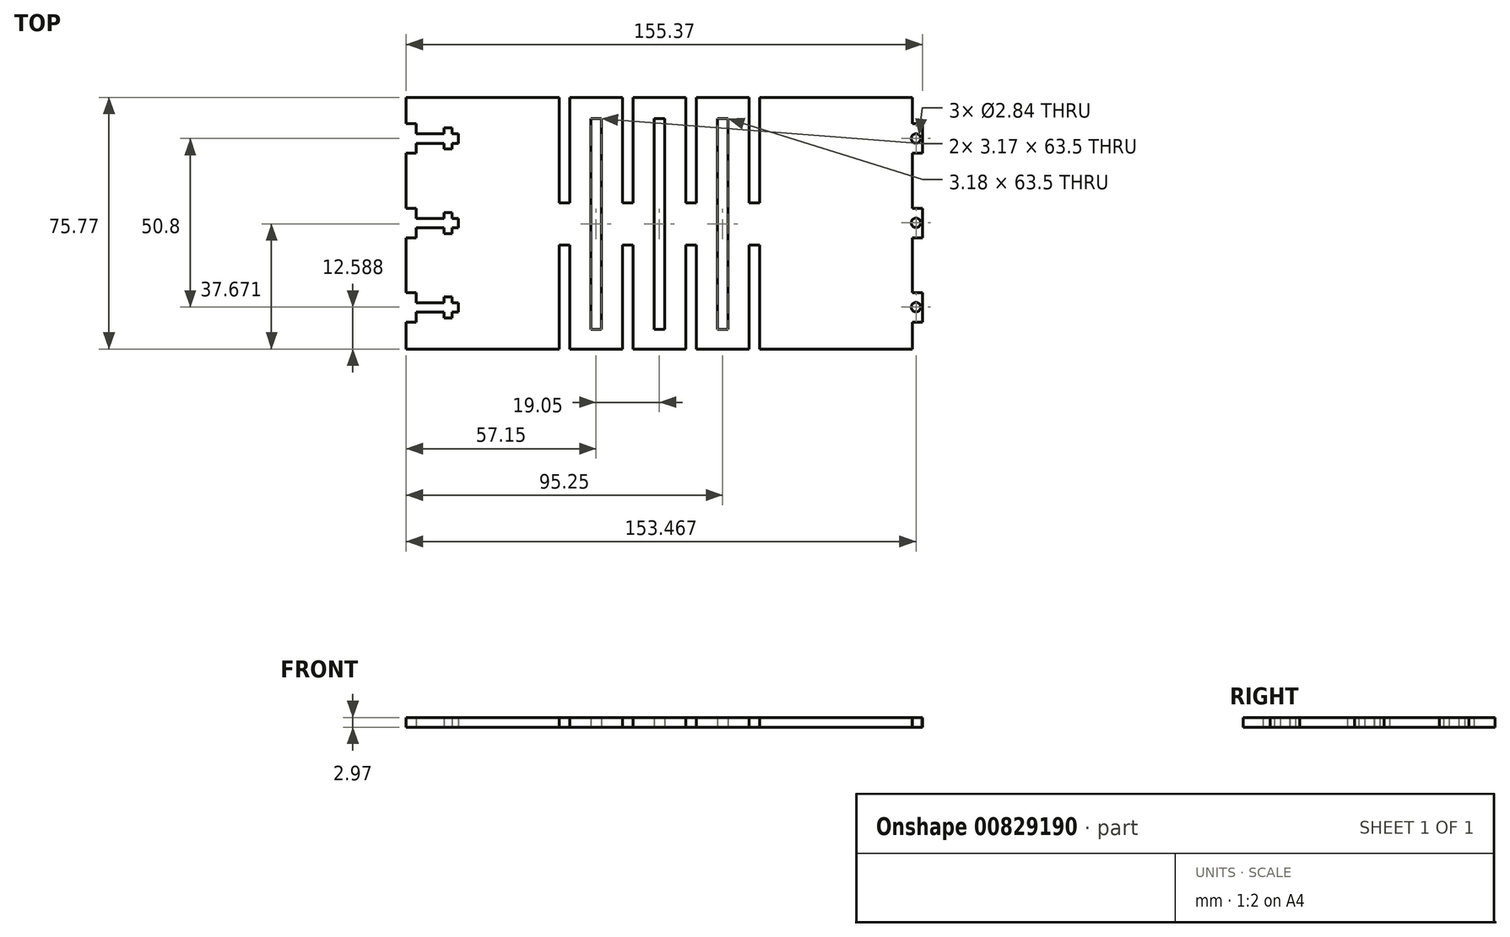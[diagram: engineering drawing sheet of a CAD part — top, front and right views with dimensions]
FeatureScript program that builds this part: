
annotation { "Feature Type Name" : "Feature", "Feature Type Description" : "" }
export const myFeature = defineFeature(function(context is Context, id is Id, definition is map)
    precondition{}
    {
        {
            var Q0;
            Q0=qCreatedBy(makeId("Top.planeOp"),FACE);
            var sketch = newSketch(context, id + "F0", { "sketchPlane" : qUnion([Q0])});
            skLineSegment(sketch, "E0.bottom", {"start": v(0, 0) * mm, "end": v(152.4, 0) * mm});
            skLineSegment(sketch, "E0.top", {"start": v(0, 75.77) * mm, "end": v(152.4, 75.77) * mm});
            skLineSegment(sketch, "E0.left", {"start": v(0, 0) * mm, "end": v(0, 8.04) * mm});
            skLineSegment(sketch, "E0.right", {"start": v(152.4, 0) * mm, "end": v(152.4, 8.04) * mm});
            skLineSegment(sketch, "E1", {"start": v(76.2, 75.77) * mm, "end": v(76.2, 0) * mm, "construction": true});
            skLineSegment(sketch, "E2.bottom", {"start": v(74.61, 69.42) * mm, "end": v(77.79, 69.42) * mm});
            skLineSegment(sketch, "E2.top", {"start": v(74.61, 5.92) * mm, "end": v(77.79, 5.92) * mm});
            skLineSegment(sketch, "E2.left", {"start": v(74.61, 69.42) * mm, "end": v(74.61, 5.92) * mm});
            skLineSegment(sketch, "E2.right", {"start": v(77.79, 69.42) * mm, "end": v(77.79, 5.92) * mm});
            skLineSegment(sketch, "E3.bottom", {"start": v(84.14, 0) * mm, "end": v(87.31, 0) * mm});
            skLineSegment(sketch, "E3.top", {"start": v(84.14, 75.77) * mm, "end": v(87.31, 75.77) * mm});
            skLineSegment(sketch, "E3.left", {"start": v(84.14, 0) * mm, "end": v(84.14, 31.32) * mm});
            skLineSegment(sketch, "E3.right", {"start": v(87.31, 0) * mm, "end": v(87.31, 31.32) * mm});
            skLineSegment(sketch, "E4", {"start": v(84.14, 31.32) * mm, "end": v(87.31, 31.32) * mm});
            skLineSegment(sketch, "E5", {"start": v(84.14, 44.02) * mm, "end": v(87.31, 44.02) * mm});
            skLineSegment(sketch, "E6.trimOffspring", {"start": v(84.14, 44.02) * mm, "end": v(84.14, 75.77) * mm});
            skLineSegment(sketch, "E7.trimOffspring", {"start": v(87.31, 44.02) * mm, "end": v(87.31, 75.77) * mm});
            skLineSegment(sketch, "E8.1.0.0", {"start": v(93.66, 69.42) * mm, "end": v(93.66, 5.92) * mm});
            skLineSegment(sketch, "E8.1.0.1", {"start": v(96.84, 69.42) * mm, "end": v(96.84, 5.92) * mm});
            skLineSegment(sketch, "E8.1.0.2", {"start": v(93.66, 5.92) * mm, "end": v(96.84, 5.92) * mm});
            skLineSegment(sketch, "E8.1.0.3", {"start": v(93.66, 69.42) * mm, "end": v(96.84, 69.42) * mm});
            skLineSegment(sketch, "E8.1.0.4", {"start": v(103.19, 44.02) * mm, "end": v(106.36, 44.02) * mm});
            skLineSegment(sketch, "E8.1.0.5", {"start": v(103.19, 44.02) * mm, "end": v(103.19, 75.77) * mm});
            skLineSegment(sketch, "E8.1.0.6", {"start": v(106.36, 44.02) * mm, "end": v(106.36, 75.77) * mm});
            skLineSegment(sketch, "E8.1.0.7", {"start": v(103.19, 75.77) * mm, "end": v(106.36, 75.77) * mm});
            skLineSegment(sketch, "E8.1.0.8", {"start": v(103.19, 31.32) * mm, "end": v(106.36, 31.32) * mm});
            skLineSegment(sketch, "E8.1.0.9", {"start": v(106.36, 0) * mm, "end": v(106.36, 31.32) * mm});
            skLineSegment(sketch, "E8.1.0.10", {"start": v(103.19, 0) * mm, "end": v(103.19, 31.32) * mm});
            skLineSegment(sketch, "E8.1.0.11", {"start": v(103.19, 0) * mm, "end": v(106.36, 0) * mm});
            skLineSegment(sketch, "E8.direction1", {"start": v(74.61, 5.92) * mm, "end": v(93.66, 5.92) * mm, "construction": true});
            skLineSegment(sketch, "E9.1.0.0", {"start": v(58.74, 69.42) * mm, "end": v(58.74, 5.92) * mm});
            skLineSegment(sketch, "E9.1.0.1", {"start": v(65.09, 31.32) * mm, "end": v(68.26, 31.32) * mm});
            skLineSegment(sketch, "E9.1.0.2", {"start": v(55.56, 69.42) * mm, "end": v(58.74, 69.42) * mm});
            skLineSegment(sketch, "E9.1.0.3", {"start": v(55.56, 69.42) * mm, "end": v(55.56, 5.92) * mm});
            skLineSegment(sketch, "E9.1.0.4", {"start": v(55.56, 5.92) * mm, "end": v(58.74, 5.92) * mm});
            skLineSegment(sketch, "E9.1.0.5", {"start": v(68.26, 0) * mm, "end": v(68.26, 31.32) * mm});
            skLineSegment(sketch, "E9.1.0.6", {"start": v(65.09, 0) * mm, "end": v(65.09, 31.32) * mm});
            skLineSegment(sketch, "E9.1.0.7", {"start": v(65.09, 0) * mm, "end": v(68.26, 0) * mm});
            skLineSegment(sketch, "E9.1.0.8", {"start": v(68.26, 44.02) * mm, "end": v(68.26, 75.77) * mm});
            skLineSegment(sketch, "E9.1.0.9", {"start": v(65.09, 44.02) * mm, "end": v(65.09, 75.77) * mm});
            skLineSegment(sketch, "E9.1.0.10", {"start": v(65.09, 44.02) * mm, "end": v(68.26, 44.02) * mm});
            skLineSegment(sketch, "E9.1.0.11", {"start": v(65.09, 75.77) * mm, "end": v(68.26, 75.77) * mm});
            skLineSegment(sketch, "E9.direction1", {"start": v(74.61, 5.92) * mm, "end": v(55.56, 5.92) * mm, "construction": true});
            skLineSegment(sketch, "E10.MirrorCS", {"start": v(49.21, 0) * mm, "end": v(46.04, 0) * mm});
            skLineSegment(sketch, "E11.MirrorCS", {"start": v(49.21, 0) * mm, "end": v(49.21, 31.32) * mm});
            skLineSegment(sketch, "E12.MirrorCS", {"start": v(46.04, 0) * mm, "end": v(46.04, 31.32) * mm});
            skLineSegment(sketch, "E13.MirrorCS", {"start": v(49.21, 31.32) * mm, "end": v(46.04, 31.32) * mm});
            skLineSegment(sketch, "E14.MirrorCS", {"start": v(49.21, 75.77) * mm, "end": v(46.04, 75.77) * mm});
            skLineSegment(sketch, "E15.MirrorCS", {"start": v(49.21, 44.02) * mm, "end": v(46.04, 44.02) * mm});
            skLineSegment(sketch, "E16.MirrorCS", {"start": v(49.21, 44.02) * mm, "end": v(49.21, 75.77) * mm});
            skLineSegment(sketch, "E17.MirrorCS", {"start": v(46.04, 44.02) * mm, "end": v(46.04, 75.77) * mm});
            skLineSegment(sketch, "E18.bottom", {"start": v(0, 67.83) * mm, "end": v(2.97, 67.83) * mm});
            skLineSegment(sketch, "E18.top", {"start": v(0, 58.94) * mm, "end": v(2.97, 58.94) * mm});
            skLineSegment(sketch, "E18.right", {"start": v(2.97, 67.83) * mm, "end": v(2.97, 64.81) * mm});
            skLineSegment(sketch, "E19", {"start": v(2.97, 63.39) * mm, "end": v(24.16, 63.39) * mm, "construction": true});
            skLineSegment(sketch, "E20.bottom", {"start": v(2.97, 64.81) * mm, "end": v(2.97, 64.81) * mm});
            skLineSegment(sketch, "E20.top", {"start": v(2.97, 61.97) * mm, "end": v(2.97, 61.97) * mm});
            skLineSegment(sketch, "E21.bottom", {"start": v(11.43, 66.56) * mm, "end": v(13.81, 66.56) * mm});
            skLineSegment(sketch, "E21.top", {"start": v(11.43, 60.21) * mm, "end": v(13.81, 60.21) * mm});
            skLineSegment(sketch, "E21.left", {"start": v(11.43, 66.56) * mm, "end": v(11.43, 64.81) * mm});
            skLineSegment(sketch, "E21.right", {"start": v(13.81, 66.56) * mm, "end": v(13.81, 64.81) * mm});
            skLineSegment(sketch, "E22.bottom", {"start": v(2.97, 64.81) * mm, "end": v(11.43, 64.81) * mm});
            skLineSegment(sketch, "E22.top", {"start": v(2.97, 61.97) * mm, "end": v(11.43, 61.97) * mm});
            skLineSegment(sketch, "E22.right", {"start": v(15.67, 64.81) * mm, "end": v(15.67, 61.97) * mm});
            skLineSegment(sketch, "E23.trimOffspring", {"start": v(2.97, 61.97) * mm, "end": v(2.97, 58.94) * mm});
            skLineSegment(sketch, "E24.trimOffspring", {"start": v(11.43, 61.97) * mm, "end": v(11.43, 60.21) * mm});
            skLineSegment(sketch, "E25.trimOffspring", {"start": v(13.81, 64.81) * mm, "end": v(15.67, 64.81) * mm});
            skLineSegment(sketch, "E26.trimOffspring", {"start": v(13.81, 61.97) * mm, "end": v(13.81, 60.21) * mm});
            skLineSegment(sketch, "E27.trimOffspring", {"start": v(13.81, 61.97) * mm, "end": v(15.67, 61.97) * mm});
            skLineSegment(sketch, "E28.0.1.0", {"start": v(0, 42.38) * mm, "end": v(2.97, 42.38) * mm});
            skLineSegment(sketch, "E28.0.1.1", {"start": v(2.97, 39.36) * mm, "end": v(11.43, 39.36) * mm});
            skLineSegment(sketch, "E28.0.1.2", {"start": v(2.97, 42.38) * mm, "end": v(2.97, 39.36) * mm});
            skLineSegment(sketch, "E28.0.1.3", {"start": v(11.43, 41.1) * mm, "end": v(11.43, 39.36) * mm});
            skLineSegment(sketch, "E28.0.1.4", {"start": v(11.43, 41.1) * mm, "end": v(13.81, 41.1) * mm});
            skLineSegment(sketch, "E28.0.1.5", {"start": v(13.81, 41.1) * mm, "end": v(13.81, 39.36) * mm});
            skLineSegment(sketch, "E28.0.1.6", {"start": v(13.81, 39.36) * mm, "end": v(15.67, 39.36) * mm});
            skLineSegment(sketch, "E28.0.1.7", {"start": v(15.67, 39.36) * mm, "end": v(15.67, 36.51) * mm});
            skLineSegment(sketch, "E28.0.1.8", {"start": v(13.81, 36.51) * mm, "end": v(15.67, 36.51) * mm});
            skLineSegment(sketch, "E28.0.1.9", {"start": v(13.81, 36.51) * mm, "end": v(13.81, 34.76) * mm});
            skLineSegment(sketch, "E28.0.1.10", {"start": v(11.43, 34.76) * mm, "end": v(13.81, 34.76) * mm});
            skLineSegment(sketch, "E28.0.1.11", {"start": v(11.43, 36.51) * mm, "end": v(11.43, 34.76) * mm});
            skLineSegment(sketch, "E28.0.1.12", {"start": v(2.97, 36.51) * mm, "end": v(11.43, 36.51) * mm});
            skLineSegment(sketch, "E28.0.1.13", {"start": v(2.97, 36.51) * mm, "end": v(2.97, 33.49) * mm});
            skLineSegment(sketch, "E28.0.1.14", {"start": v(0, 33.49) * mm, "end": v(2.97, 33.49) * mm});
            skLineSegment(sketch, "E28.0.2.0", {"start": v(0, 16.93) * mm, "end": v(2.97, 16.93) * mm});
            skLineSegment(sketch, "E28.0.2.1", {"start": v(2.97, 13.9) * mm, "end": v(11.43, 13.9) * mm});
            skLineSegment(sketch, "E28.0.2.2", {"start": v(2.97, 16.93) * mm, "end": v(2.97, 13.9) * mm});
            skLineSegment(sketch, "E28.0.2.3", {"start": v(11.43, 15.66) * mm, "end": v(11.43, 13.9) * mm});
            skLineSegment(sketch, "E28.0.2.4", {"start": v(11.43, 15.66) * mm, "end": v(13.81, 15.66) * mm});
            skLineSegment(sketch, "E28.0.2.5", {"start": v(13.81, 15.66) * mm, "end": v(13.81, 13.9) * mm});
            skLineSegment(sketch, "E28.0.2.6", {"start": v(13.81, 13.9) * mm, "end": v(15.67, 13.9) * mm});
            skLineSegment(sketch, "E28.0.2.7", {"start": v(15.67, 13.9) * mm, "end": v(15.67, 11.06) * mm});
            skLineSegment(sketch, "E28.0.2.8", {"start": v(13.81, 11.06) * mm, "end": v(15.67, 11.06) * mm});
            skLineSegment(sketch, "E28.0.2.9", {"start": v(13.81, 11.06) * mm, "end": v(13.81, 9.3) * mm});
            skLineSegment(sketch, "E28.0.2.10", {"start": v(11.43, 9.3) * mm, "end": v(13.81, 9.3) * mm});
            skLineSegment(sketch, "E28.0.2.11", {"start": v(11.43, 11.06) * mm, "end": v(11.43, 9.3) * mm});
            skLineSegment(sketch, "E28.0.2.12", {"start": v(2.97, 11.06) * mm, "end": v(11.43, 11.06) * mm});
            skLineSegment(sketch, "E28.0.2.13", {"start": v(2.97, 11.06) * mm, "end": v(2.97, 8.04) * mm});
            skLineSegment(sketch, "E28.0.2.14", {"start": v(0, 8.04) * mm, "end": v(2.97, 8.04) * mm});
            skLineSegment(sketch, "E28.direction1", {"start": v(0, 67.83) * mm, "end": v(25.4, 67.83) * mm, "construction": true});
            skLineSegment(sketch, "E28.direction2", {"start": v(0, 58.94) * mm, "end": v(0, 42.38) * mm, "construction": true});
            skLineSegment(sketch, "E29.trimOffspring", {"start": v(0, 67.83) * mm, "end": v(0, 75.77) * mm});
            skLineSegment(sketch, "E30.trimOffspring", {"start": v(0, 42.38) * mm, "end": v(0, 58.94) * mm});
            skLineSegment(sketch, "E31.trimOffspring", {"start": v(0, 16.93) * mm, "end": v(0, 33.49) * mm});
            skLineSegment(sketch, "E32.1.0.0", {"start": v(155.37, 67.83) * mm, "end": v(155.37, 64.81) * mm});
            skLineSegment(sketch, "E32.1.0.1", {"start": v(152.4, 67.83) * mm, "end": v(155.37, 67.83) * mm});
            skLineSegment(sketch, "E32.1.0.2", {"start": v(155.37, 61.97) * mm, "end": v(155.37, 58.94) * mm});
            skLineSegment(sketch, "E32.1.0.3", {"start": v(152.4, 58.94) * mm, "end": v(155.37, 58.94) * mm});
            skLineSegment(sketch, "E32.1.0.4", {"start": v(152.4, 42.38) * mm, "end": v(155.37, 42.38) * mm});
            skLineSegment(sketch, "E32.1.0.5", {"start": v(155.37, 42.38) * mm, "end": v(155.37, 39.36) * mm});
            skLineSegment(sketch, "E32.1.0.6", {"start": v(155.37, 36.51) * mm, "end": v(155.37, 33.49) * mm});
            skLineSegment(sketch, "E32.1.0.7", {"start": v(152.4, 33.49) * mm, "end": v(155.37, 33.49) * mm});
            skLineSegment(sketch, "E32.1.0.8", {"start": v(152.4, 16.93) * mm, "end": v(155.37, 16.93) * mm});
            skLineSegment(sketch, "E32.1.0.9", {"start": v(155.37, 16.93) * mm, "end": v(155.37, 13.9) * mm});
            skLineSegment(sketch, "E32.1.0.10", {"start": v(155.37, 11.06) * mm, "end": v(155.37, 8.04) * mm});
            skLineSegment(sketch, "E32.1.0.11", {"start": v(152.4, 8.04) * mm, "end": v(155.37, 8.04) * mm});
            skLineSegment(sketch, "E32.direction1", {"start": v(2.97, 64.81) * mm, "end": v(155.37, 64.81) * mm, "construction": true});
            skLineSegment(sketch, "E33", {"start": v(155.37, 64.81) * mm, "end": v(155.37, 61.97) * mm});
            skLineSegment(sketch, "E34", {"start": v(155.37, 39.36) * mm, "end": v(155.37, 36.51) * mm});
            skLineSegment(sketch, "E35", {"start": v(155.37, 13.9) * mm, "end": v(155.37, 11.06) * mm});
            skCircle(sketch, "E36", {"center": v(153.47, 63.39) * mm, "radius": 1.42 * mm});
            skCircle(sketch, "E37.0.1.0", {"center": v(153.47, 37.99) * mm, "radius": 1.42 * mm});
            skCircle(sketch, "E37.0.2.0", {"center": v(153.47, 12.59) * mm, "radius": 1.42 * mm});
            skLineSegment(sketch, "E37.direction1", {"start": v(153.47, 63.39) * mm, "end": v(178.87, 63.39) * mm, "construction": true});
            skLineSegment(sketch, "E37.direction2", {"start": v(153.47, 63.39) * mm, "end": v(153.47, 37.99) * mm, "construction": true});
            skLineSegment(sketch, "E38.trimOffspring", {"start": v(152.4, 67.83) * mm, "end": v(152.4, 75.77) * mm});
            skLineSegment(sketch, "E39.trimOffspring", {"start": v(152.4, 42.38) * mm, "end": v(152.4, 58.94) * mm});
            skLineSegment(sketch, "E40.trimOffspring", {"start": v(152.4, 16.93) * mm, "end": v(152.4, 33.49) * mm});
            skSolve(sketch);
        }
        {
            var Q0;
            {var subQ16=sQuery(id+"F0.wireOp",EDGE,"E0.left");Q0=makeQuery(id+"F0.imprint","IMPRINT",FACE,{"disambiguationData":[TD([[makeQuery(id+"F0.imprint","IMPRINT",EDGE,{"derivedFrom":subQ16}),-1.0]])]});}
            var Q1;
            Q1=makeQuery(id+"F0.imprint","IMPRINT",FACE,{"disambiguationData":[TD([[makeQuery(id+"F0.imprint","IMPRINT",EDGE,{"derivedFrom":sQuery(id+"F0.wireOp",EDGE,"E32.1.0.0")}),-1.0]])]});
            var Q2;
            {var subQ0=sQuery(id+"F0.wireOp",EDGE,"E32.1.0.4");Q2=makeQuery(id+"F0.imprint","IMPRINT",FACE,{"disambiguationData":[TD([[makeQuery(id+"F0.imprint","IMPRINT",EDGE,{"derivedFrom":subQ0}),-1.0]])]});}
            var Q3;
            {var subQ0=sQuery(id+"F0.wireOp",EDGE,"E32.1.0.8");Q3=makeQuery(id+"F0.imprint","IMPRINT",FACE,{"disambiguationData":[TD([[makeQuery(id+"F0.imprint","IMPRINT",EDGE,{"derivedFrom":subQ0}),-1.0]])]});}
            extrude(context, id + "F1", {"entities" : qUnion([Q0, Q1, Q2, Q3]), "depth" : 2.97 * mm, "offsetDistance" : 25.4 * mm});
        }
    });
